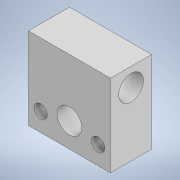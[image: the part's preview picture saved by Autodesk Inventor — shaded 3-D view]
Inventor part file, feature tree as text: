
AUTODESK INVENTOR PART (.ipt)
format: ipt  version: 2022 (Build 260153070, 153G)  size: 119,296 bytes
history: native  units: mm
features: extrude x3, sketch x3
ambient origin geometry x8: Origin, YZ Plane, XZ Plane, XY Plane, X Axis, Y Axis, Z Axis, Center Point
bodies: Solid1 (feature_tree)
feature tree (6):
  extrude  "Extrusion1"  Depth=10.0mm
  sketch  "Sketch2"  dims[d2=10.0mm d3=10.0mm]
  extrude  "Extrusion2"  Depth=10.0mm
  extrude  "Extrusion3"  Depth=10.0mm
  sketch  "Sketch1"  dims[d0=20.0mm d1=10.0mm]
  sketch  "Sketch3"  dims[d4=10.0mm d5=0.0mm d6=6.0mm d7=4.0mm d8=3.2mm d9=7.0mm d10=5.5mm d11=6.05mm d12=5.0mm d13=15.5mm d14=20.0mm d15=0.0mm d16=10.0mm d17=0.0mm]
